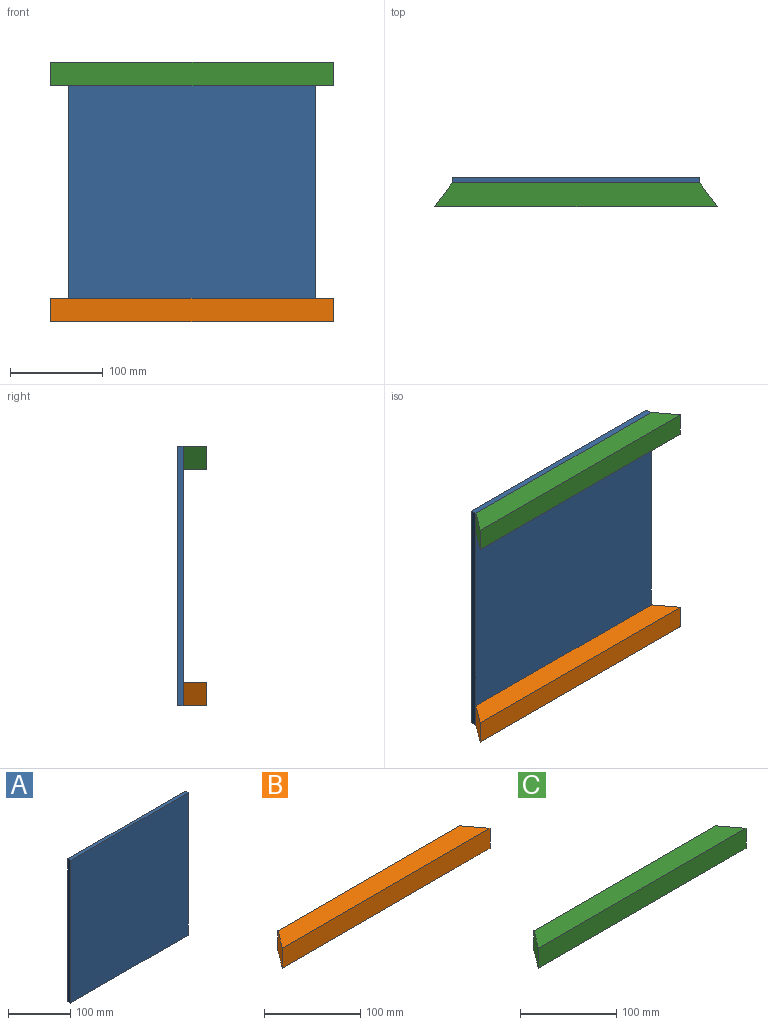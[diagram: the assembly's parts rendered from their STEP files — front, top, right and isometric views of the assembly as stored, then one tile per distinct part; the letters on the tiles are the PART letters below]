
ASSEMBLY  parts=3 mates=1
PART A: 6 faces, bbox 266.7x6.4x279.4 mm
  f0: plane 279.4x6.35mm, normal (-1,0,0), area 1774.2mm2, adj f1,f3,f4,f5
  f1: plane 266.7x6.35mm, normal (0,0,1), area 1693.5mm2, adj f0,f2,f4,f5
  f2: plane 279.4x6.35mm, normal (1,0,0), area 1774.2mm2, adj f1,f3,f4,f5
  f3: plane 266.7x6.35mm, normal (0,0,-1), area 1693.5mm2, adj f0,f2,f4,f5
  f4: plane 279.4x266.7mm, normal (0,1,0), area 74516mm2, adj f0,f1,f2,f3
  f5: plane 279.4x266.7mm, normal (0,-1,0), area 74516mm2, adj f0,f1,f2,f3
PART B: 6 faces, bbox 304.8x25.4x25.4 mm
  f0: plane 25.4x25.4mm, normal (-0.8,0.6,0), area 806.5mm2, adj f1,f3,f4,f5
  f1: plane 304.8x25.4mm, normal (0,-1,0), area 7741.9mm2, adj f0,f2,f4,f5
  f2: plane 25.4x25.4mm, normal (0.8,0.6,0), area 806.5mm2, adj f1,f3,f4,f5
  f3: plane 266.7x25.4mm, normal (0,1,0), area 6774.2mm2, adj f0,f2,f4,f5
  f4: plane 304.8x25.4mm, normal (0,0,1), area 7258.1mm2, adj f0,f1,f2,f3
  f5: plane 304.8x25.4mm, normal (0,0,-1), area 7258.1mm2, adj f0,f1,f2,f3
PART C: 6 faces, bbox 304.8x25.4x25.4 mm
  f0: plane 25.4x25.4mm, normal (-0.8,0.6,0), area 806.4mm2, adj f1,f3,f4,f5
  f1: plane 304.8x25.4mm, normal (0,-1,0), area 7741.9mm2, adj f0,f2,f4,f5
  f2: plane 25.4x25.4mm, normal (0.8,0.6,0), area 806.4mm2, adj f1,f3,f4,f5
  f3: plane 266.7x25.4mm, normal (0,1,0), area 6774.2mm2, adj f0,f2,f4,f5
  f4: plane 304.8x25.4mm, normal (0,0,1), area 7258.1mm2, adj f0,f1,f2,f3
  f5: plane 304.8x25.4mm, normal (0,0,-1), area 7258.1mm2, adj f0,f1,f2,f3
PLACE A at identity
PLACE B t=(-13.69,-21.79,-254)mm
PLACE C at identity
MATE fastened B.f3 <-> A.f5  axis (0,1,0) through (-36.1,26.88,-241.3)mm
